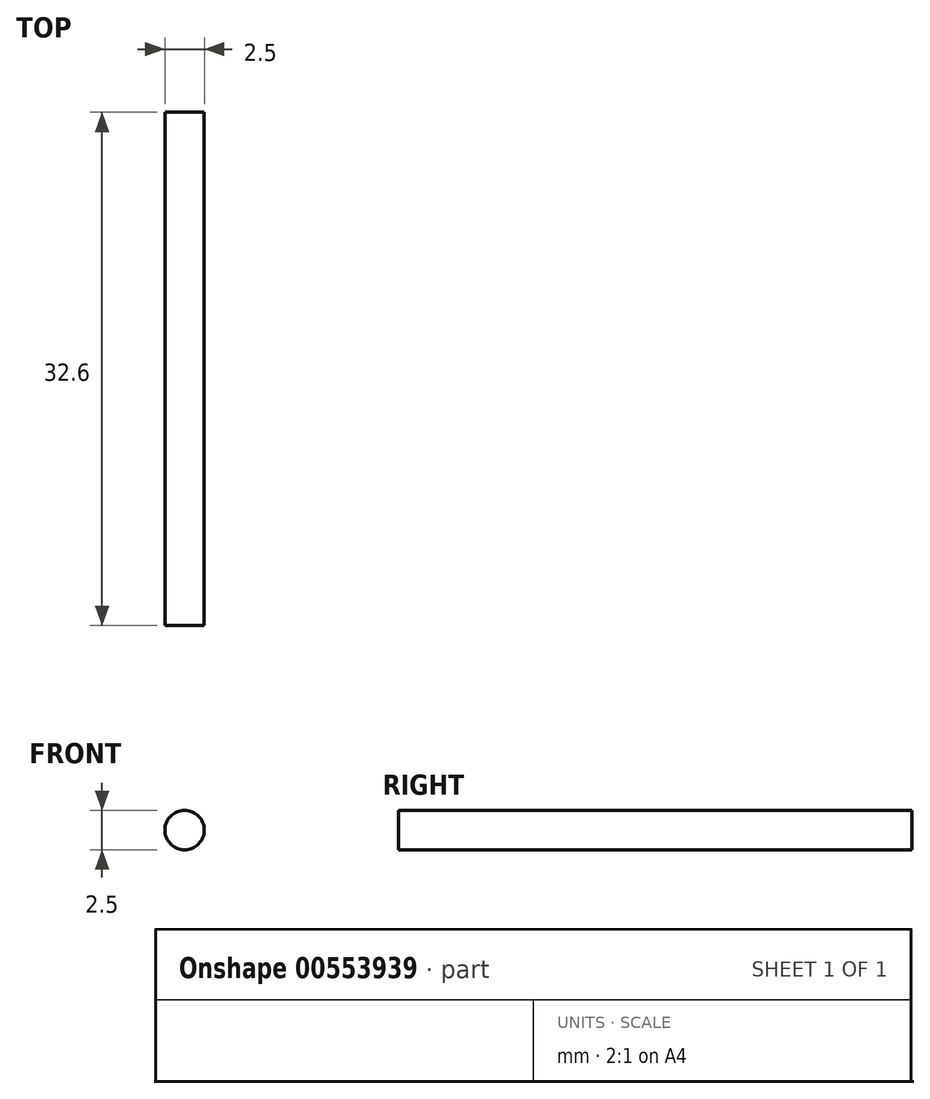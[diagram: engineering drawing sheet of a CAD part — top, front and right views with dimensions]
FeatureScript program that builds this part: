
annotation { "Feature Type Name" : "Feature", "Feature Type Description" : "" }
export const myFeature = defineFeature(function(context is Context, id is Id, definition is map)
    precondition{}
    {
        {
            var Q0;
            Q0=qCreatedBy(makeId("Front.planeOp"),FACE);
            var sketch = newSketch(context, id + "F0", { "sketchPlane" : qUnion([Q0])});
            skCircle(sketch, "E0", {"center": v(-35.83, 12.89) * mm, "radius": 1.25 * mm});
            skSolve(sketch);
        }
        {
            var Q0;
            Q0=makeQuery(id+"F0.imprint","IMPRINT",FACE,{"disambiguationData":[TD([[makeQuery(id+"F0.imprint","IMPRINT",EDGE,{"derivedFrom":sQuery(id+"F0.wireOp",EDGE,"E0")}),1.0]])]});
            extrude(context, id + "F1", {"entities" : qUnion([Q0]), "oppositeDirection" : true, "depth" : 32.6 * mm, "offsetDistance" : 25 * mm});
        }
    });
